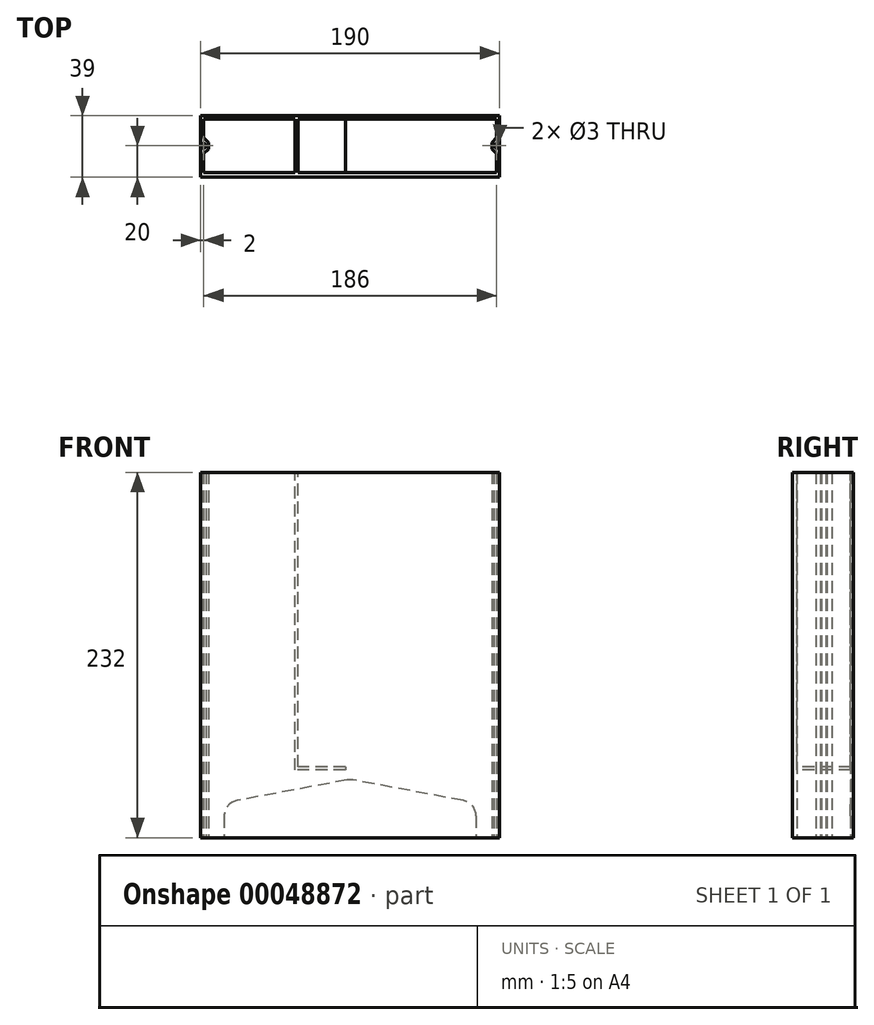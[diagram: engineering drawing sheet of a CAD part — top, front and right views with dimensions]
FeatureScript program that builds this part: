
annotation { "Feature Type Name" : "Feature", "Feature Type Description" : "" }
export const myFeature = defineFeature(function(context is Context, id is Id, definition is map)
    precondition{}
    {
        {
            var Q0;
            Q0=qCreatedBy(makeId("Top.planeOp"),FACE);
            var sketch = newSketch(context, id + "F0", { "sketchPlane" : qUnion([Q0])});
            skLineSegment(sketch, "E0.bottom", {"start": v(0, 0) * mm, "end": v(190, 0) * mm});
            skLineSegment(sketch, "E0.top", {"start": v(0, 39) * mm, "end": v(190, 39) * mm});
            skLineSegment(sketch, "E0.left", {"start": v(0, 0) * mm, "end": v(0, 39) * mm});
            skLineSegment(sketch, "E0.right", {"start": v(190, 0) * mm, "end": v(190, 39) * mm});
            skLineSegment(sketch, "E1.bottom", {"start": v(2, 3) * mm, "end": v(188, 3) * mm});
            skLineSegment(sketch, "E1.top", {"start": v(2, 37) * mm, "end": v(188, 37) * mm});
            skLineSegment(sketch, "E2", {"start": v(2, 37) * mm, "end": v(2, 25.12) * mm});
            skLineSegment(sketch, "E3", {"start": v(2, 25.12) * mm, "end": v(5, 22.12) * mm});
            skLineSegment(sketch, "E4", {"start": v(5, 22.12) * mm, "end": v(5, 17.88) * mm});
            skLineSegment(sketch, "E5", {"start": v(5, 17.88) * mm, "end": v(2, 14.88) * mm});
            skLineSegment(sketch, "E6", {"start": v(2, 14.88) * mm, "end": v(2, 3) * mm});
            skLineSegment(sketch, "E7", {"start": v(2, 25.12) * mm, "end": v(2, 14.88) * mm, "construction": true});
            skCircle(sketch, "E8", {"center": v(2, 20) * mm, "radius": 1.5 * mm});
            skLineSegment(sketch, "E9", {"start": v(95, 37) * mm, "end": v(95, 3) * mm, "construction": true});
            skLineSegment(sketch, "E10.MirrorCS", {"start": v(188, 14.88) * mm, "end": v(188, 3) * mm});
            skLineSegment(sketch, "E11.MirrorCS", {"start": v(185, 17.88) * mm, "end": v(188, 14.88) * mm});
            skLineSegment(sketch, "E12.MirrorCS", {"start": v(185, 22.12) * mm, "end": v(185, 17.88) * mm});
            skCircle(sketch, "E13.MirrorC", {"center": v(188, 20) * mm, "radius": 1.5 * mm});
            skLineSegment(sketch, "E14.MirrorCS", {"start": v(188, 37) * mm, "end": v(188, 25.12) * mm});
            skLineSegment(sketch, "E15.MirrorCS", {"start": v(188, 25.12) * mm, "end": v(185, 22.12) * mm});
            skSolve(sketch);
        }
        {
            var Q0;
            Q0=makeQuery(id+"F0.imprint","IMPRINT",FACE,{"disambiguationData":[TD([[makeQuery(id+"F0.imprint","IMPRINT",EDGE,{"derivedFrom":sQuery(id+"F0.wireOp",EDGE,"E0.bottom")}),1.0]])]});
            extrude(context, id + "F1", {"entities" : qUnion([Q0]), "depth" : 232 * mm});
        }
        {
            var Q0;
            Q0=makeQuery(id+"F1.opExtrude","SWEPT_FACE",FACE,{"disambiguationData":[OSD([sQuery(id+"F0.wireOp",EDGE,"E0.bottom")])]});
            var sketch = newSketch(context, id + "F2", { "sketchPlane" : qUnion([Q0])});
            skLineSegment(sketch, "E16.bottom", {"start": v(60, 232) * mm, "end": v(62, 232) * mm});
            skLineSegment(sketch, "E16.top", {"start": v(60, 43) * mm, "end": v(62, 43) * mm});
            skLineSegment(sketch, "E16.left", {"start": v(60, 232) * mm, "end": v(60, 43) * mm});
            skLineSegment(sketch, "E16.right", {"start": v(62, 232) * mm, "end": v(62, 43) * mm});
            skLineSegment(sketch, "E17.bottom", {"start": v(60, 43) * mm, "end": v(92, 43) * mm});
            skLineSegment(sketch, "E17.top", {"start": v(60, 45) * mm, "end": v(92, 45) * mm});
            skLineSegment(sketch, "E17.left", {"start": v(60, 43) * mm, "end": v(60, 45) * mm});
            skLineSegment(sketch, "E17.right", {"start": v(92, 43) * mm, "end": v(92, 45) * mm});
            skSolve(sketch);
        }
        {
            var Q0;
            Q0=qSketchRegion(id+"F2",true);
            extrude(context, id + "F3", {"entities" : qUnion([Q0]), "operationType" : NewBodyOperationType.ADD, "oppositeDirection" : true, "depth" : 39 * mm});
        }
        {
            var Q0;
            Q0=makeQuery(id+"F1.opExtrude","SWEPT_FACE",FACE,{"disambiguationData":[OSD([sQuery(id+"F0.wireOp",EDGE,"E0.top")])]});
            var sketch = newSketch(context, id + "F4", { "sketchPlane" : qUnion([Q0])});
            skLineSegment(sketch, "E18.bottom", {"start": v(-175, 22) * mm, "end": v(-15, 22) * mm});
            skLineSegment(sketch, "E18.top", {"start": v(-175, 0) * mm, "end": v(-15, 0) * mm});
            skLineSegment(sketch, "E18.left", {"start": v(-175, 22) * mm, "end": v(-175, 0) * mm});
            skLineSegment(sketch, "E18.right", {"start": v(-15, 22) * mm, "end": v(-15, 0) * mm});
            skLineSegment(sketch, "E19", {"start": v(-175, 22) * mm, "end": v(-95, 37) * mm});
            skLineSegment(sketch, "E20", {"start": v(-95, 37) * mm, "end": v(-15, 22) * mm});
            skSolve(sketch);
        }
        {
            var Q0;
            Q0 = qSketchRegion(id + "F4", true);
            extrude(context, id + "F5", {"entities" : qUnion([Q0]), "operationType" : NewBodyOperationType.REMOVE, "oppositeDirection" : true, "depth" : 5 * mm});
        }
        {
            var Q0;
            Q0=makeQuery(id+"F5.boolean.opBoolean","COPY",EDGE,{"derivedFrom":makeQuery(id+"F5.opExtrude","SWEPT_EDGE",EDGE,{"disambiguationData":[OSD([sQuery(id+"F4.wireOp",EDGE,"E18.bottom"),sQuery(id+"F4.wireOp",EDGE,"E18.left"),sQuery(id+"F4.wireOp",EDGE,"7e61b8fc-968f-4950-85b5-5346b5c98c3d")])]})});
            var Q1;
            Q1=makeQuery(id+"F5.boolean.opBoolean","COPY",EDGE,{"derivedFrom":makeQuery(id+"F5.opExtrude","SWEPT_EDGE",EDGE,{"disambiguationData":[OSD([sQuery(id+"F4.wireOp",EDGE,"E18.bottom"),sQuery(id+"F4.wireOp",EDGE,"E18.right"),sQuery(id+"F4.wireOp",EDGE,"7e61b8fc-968f-4950-85b5-5346b5c98c3d")])]})});
            var Q2;
            Q2=makeQuery(id+"F5.boolean.opBoolean","COPY",EDGE,{"derivedFrom":makeQuery(id+"F5.opExtrude","SWEPT_EDGE",EDGE,{"disambiguationData":[OSD([sQuery(id+"F4.wireOp",EDGE,"E19"),sQuery(id+"F4.wireOp",EDGE,"E20")])]})});
            fillet(context, id + "F6", {"entities" : qUnion([Q0, Q1, Q2]), "radius" : 10 * mm, "tangentPropagation" : true, "allowEdgeOverflow" : false});
        }
    });
